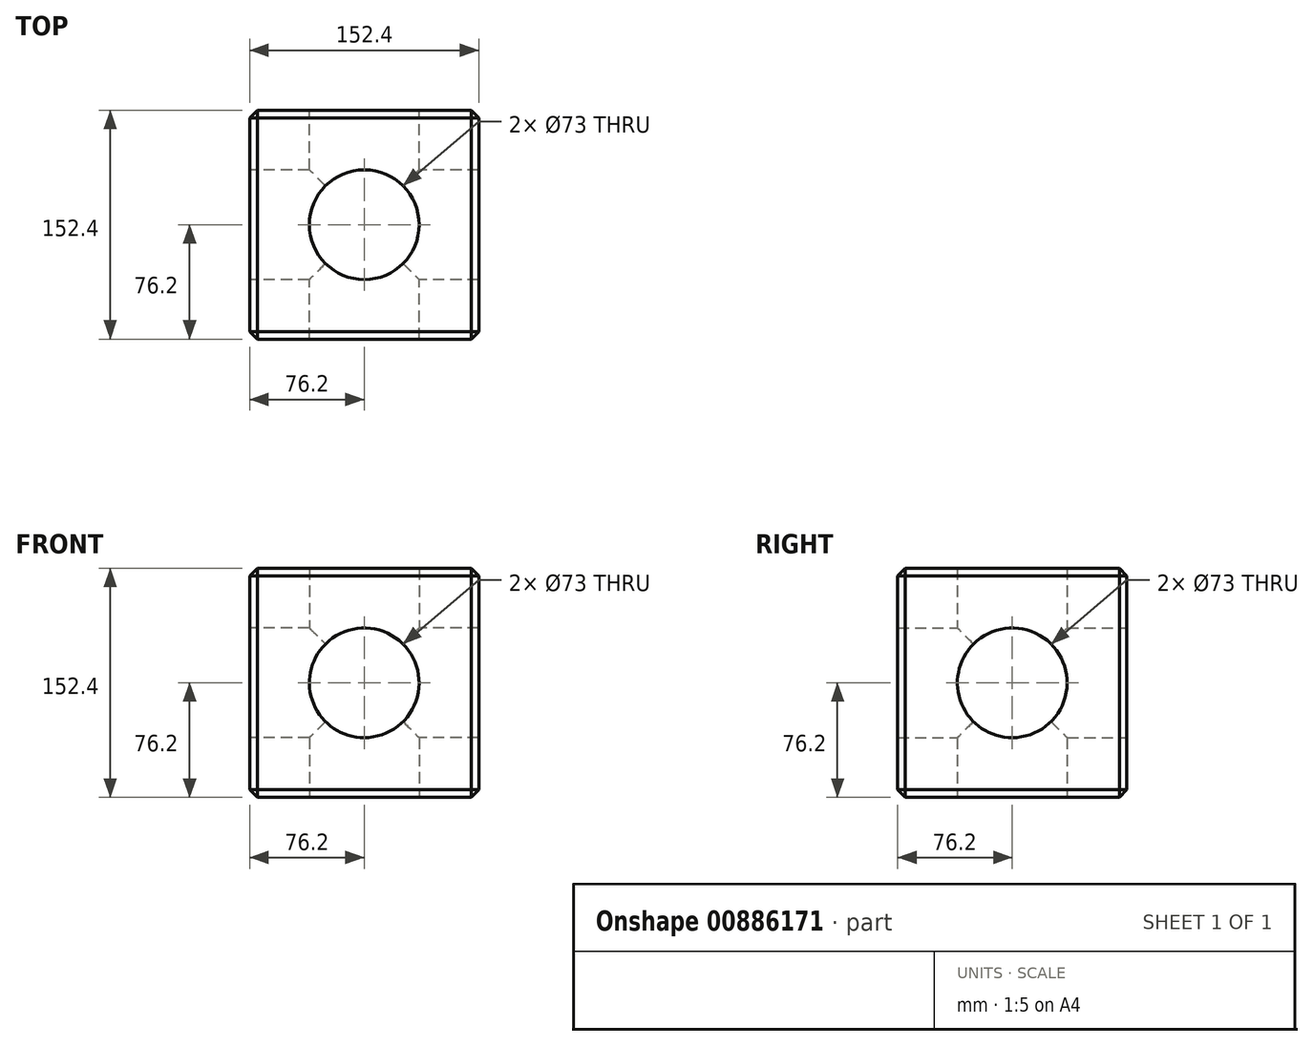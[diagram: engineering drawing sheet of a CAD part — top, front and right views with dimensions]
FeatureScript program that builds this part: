
annotation { "Feature Type Name" : "Feature", "Feature Type Description" : "" }
export const myFeature = defineFeature(function(context is Context, id is Id, definition is map)
    precondition{}
    {
        {
            var Q0;
            Q0=qCreatedBy(makeId("Front.planeOp"),FACE);
            var sketch = newSketch(context, id + "F0", { "sketchPlane" : qUnion([Q0])});
            skLineSegment(sketch, "E0.bottom", {"start": v(-76.2, 76.2) * mm, "end": v(76.2, 76.2) * mm});
            skLineSegment(sketch, "E0.top", {"start": v(-76.2, -76.2) * mm, "end": v(76.2, -76.2) * mm});
            skLineSegment(sketch, "E0.left", {"start": v(-76.2, 76.2) * mm, "end": v(-76.2, -76.2) * mm});
            skLineSegment(sketch, "E0.right", {"start": v(76.2, 76.2) * mm, "end": v(76.2, -76.2) * mm});
            skSolve(sketch);
        }
        {
            var Q0;
            Q0=makeQuery(id+"F0.imprint","IMPRINT",FACE,{"disambiguationData":[TD([[makeQuery(id+"F0.imprint","IMPRINT",EDGE,{"derivedFrom":sQuery(id+"F0.wireOp",EDGE,"E0.bottom")}),-1.0]])]});
            extrude(context, id + "F1", {"entities" : qUnion([Q0]), "depth" : 152.4 * mm, "offsetDistance" : 25.4 * mm});
        }
        {
            var Q0;
            Q0=makeQuery(id+"F1.opExtrude","CAP_EDGE",EDGE,{"disambiguationData":[OSD([sQuery(id+"F0.wireOp",EDGE,"E0.bottom")])],"isStart":false});
            var Q1;
            Q1=makeQuery(id+"F1.opExtrude","SWEPT_EDGE",EDGE,{"disambiguationData":[OSD([sQuery(id+"F0.wireOp",EDGE,"E0.bottom"),sQuery(id+"F0.wireOp",EDGE,"E0.left")])]});
            var Q2;
            Q2=makeQuery(id+"F1.opExtrude","SWEPT_EDGE",EDGE,{"disambiguationData":[OSD([sQuery(id+"F0.wireOp",EDGE,"E0.bottom"),sQuery(id+"F0.wireOp",EDGE,"E0.right")])]});
            var Q3;
            Q3=makeQuery(id+"F1.opExtrude","CAP_EDGE",EDGE,{"disambiguationData":[OSD([sQuery(id+"F0.wireOp",EDGE,"E0.bottom")])],"isStart":true});
            var Q4;
            Q4=makeQuery(id+"F1.opExtrude","CAP_EDGE",EDGE,{"disambiguationData":[OSD([sQuery(id+"F0.wireOp",EDGE,"E0.right")])],"isStart":false});
            var Q5;
            Q5=makeQuery(id+"F1.opExtrude","CAP_EDGE",EDGE,{"disambiguationData":[OSD([sQuery(id+"F0.wireOp",EDGE,"E0.left")])],"isStart":false});
            var Q6;
            Q6=makeQuery(id+"F1.opExtrude","CAP_EDGE",EDGE,{"disambiguationData":[OSD([sQuery(id+"F0.wireOp",EDGE,"E0.top")])],"isStart":false});
            var Q7;
            Q7=makeQuery(id+"F1.opExtrude","SWEPT_EDGE",EDGE,{"disambiguationData":[OSD([sQuery(id+"F0.wireOp",EDGE,"E0.top"),sQuery(id+"F0.wireOp",EDGE,"E0.right")])]});
            var Q8;
            Q8=makeQuery(id+"F1.opExtrude","CAP_EDGE",EDGE,{"disambiguationData":[OSD([sQuery(id+"F0.wireOp",EDGE,"E0.right")])],"isStart":true});
            var Q9;
            Q9=makeQuery(id+"F1.opExtrude","CAP_EDGE",EDGE,{"disambiguationData":[OSD([sQuery(id+"F0.wireOp",EDGE,"E0.left")])],"isStart":true});
            var Q10;
            Q10=makeQuery(id+"F1.opExtrude","CAP_EDGE",EDGE,{"disambiguationData":[OSD([sQuery(id+"F0.wireOp",EDGE,"E0.top")])],"isStart":true});
            var Q11;
            Q11=makeQuery(id+"F1.opExtrude","SWEPT_EDGE",EDGE,{"disambiguationData":[OSD([sQuery(id+"F0.wireOp",EDGE,"E0.top"),sQuery(id+"F0.wireOp",EDGE,"E0.left")])]});
            chamfer(context, id + "F2", {"entities" : qUnion([Q0, Q1, Q2, Q3, Q4, Q5, Q6, Q7, Q8, Q9, Q10, Q11]), "width" : 5 * mm, "tangentPropagation" : true});
        }
        {
            var Q0;
            Q0=makeQuery(id+"F1.opExtrude","CAP_FACE",FACE,{"disambiguationData":[OSD([sQuery(id+"F0.wireOp",EDGE,"E0.bottom"),sQuery(id+"F0.wireOp",EDGE,"E0.top"),sQuery(id+"F0.wireOp",EDGE,"E0.left"),sQuery(id+"F0.wireOp",EDGE,"E0.right")])],"isStart":true});
            var sketch = newSketch(context, id + "F3", { "sketchPlane" : qUnion([Q0])});
            skCircle(sketch, "E1", {"center": v(0, 0) * mm, "radius": 36.5 * mm});
            skLineSegment(sketch, "E2", {"start": v(71.2, -71.2) * mm, "end": v(-71.2, 71.2) * mm, "construction": true});
            skSolve(sketch);
        }
        {
            var Q0;
            Q0=makeQuery(id+"F3.imprint","IMPRINT",FACE,{"disambiguationData":[TD([[makeQuery(id+"F3.imprint","IMPRINT",EDGE,{"derivedFrom":sQuery(id+"F3.wireOp",EDGE,"E1")}),1.0]])]});
            extrude(context, id + "F4", {"entities" : qUnion([Q0]), "operationType" : NewBodyOperationType.REMOVE, "endBound" : BoundingType.THROUGH_ALL, "oppositeDirection" : true, "depth" : 25 * mm, "offsetDistance" : 25 * mm});
        }
        {
            var Q0;
            Q0=makeQuery(id+"F1.opExtrude","SWEPT_FACE",FACE,{"disambiguationData":[OSD([sQuery(id+"F0.wireOp",EDGE,"E0.top")])]});
            var sketch = newSketch(context, id + "F5", { "sketchPlane" : qUnion([Q0])});
            skPoint(sketch, "E3", {"position": v(0, 76.2) * mm});
            skLineSegment(sketch, "E4", {"start": v(-71.2, 147.4) * mm, "end": v(71.2, 5) * mm, "construction": true});
            skSolve(sketch);
        }
        {
            var Q0;
            Q0=makeQuery(id+"F1.opExtrude","SWEPT_FACE",FACE,{"disambiguationData":[OSD([sQuery(id+"F0.wireOp",EDGE,"E0.left")])]});
            var sketch = newSketch(context, id + "F6", { "sketchPlane" : qUnion([Q0])});
            skPoint(sketch, "E5", {"position": v(76.2, 0) * mm});
            skLineSegment(sketch, "E6", {"start": v(147.4, 71.2) * mm, "end": v(5, -71.2) * mm, "construction": true});
            skSolve(sketch);
        }
        {
            var Q0;
            Q0=sQuery(id+"F6.wireOp",VERTEX,"E5");
            var Q1;
            Q1=sQuery(id+"F5.wireOp",VERTEX,"E3");
            var Q2;
            Q2=makeQuery(id+"F1.opExtrude","SWEPT_BODY",BODY,{"disambiguationData":[OSD([sQuery(id+"F0.wireOp",EDGE,"E0.bottom"),sQuery(id+"F0.wireOp",EDGE,"E0.top"),sQuery(id+"F0.wireOp",EDGE,"E0.left"),sQuery(id+"F0.wireOp",EDGE,"E0.right")])]});
            hole(context, id + "F7", {"style" : HoleStyle.SIMPLE, "endStyle" : HoleEndStyle.THROUGH, "holeDiameter" : 73 * mm, "majorDiameter" : 5 * mm, "isTappedThrough" : true, "tappedDepth" : 12 * mm, "tapClearance" : 3, "locations" : qUnion([Q0, Q1]), "scope" : qUnion([Q2])});
        }
    });
